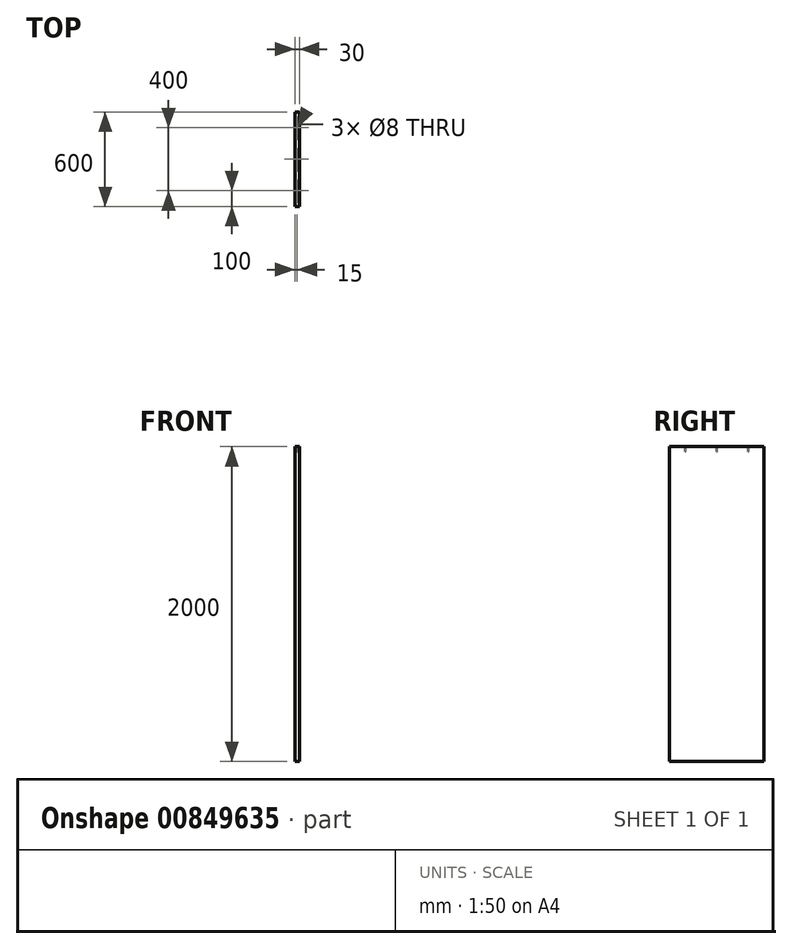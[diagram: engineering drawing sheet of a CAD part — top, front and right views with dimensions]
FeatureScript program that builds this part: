
annotation { "Feature Type Name" : "Feature", "Feature Type Description" : "" }
export const myFeature = defineFeature(function(context is Context, id is Id, definition is map)
    precondition{}
    {
        {
            var Q0;
            Q0=qCreatedBy(makeId("Right.planeOp"),FACE);
            var sketch = newSketch(context, id + "F0", { "sketchPlane" : qUnion([Q0])});
            skLineSegment(sketch, "E0.bottom", {"start": v(-600, 1000) * mm, "end": v(0, 1000) * mm});
            skLineSegment(sketch, "E0.top", {"start": v(-600, -1000) * mm, "end": v(0, -1000) * mm});
            skLineSegment(sketch, "E0.left", {"start": v(-600, 1000) * mm, "end": v(-600, -1000) * mm});
            skLineSegment(sketch, "E0.right", {"start": v(0, 1000) * mm, "end": v(0, -1000) * mm});
            skSolve(sketch);
        }
        {
            var Q0;
            Q0=makeQuery(id+"F0.imprint","IMPRINT",FACE,{"disambiguationData":[TD([[makeQuery(id+"F0.imprint","IMPRINT",EDGE,{"derivedFrom":sQuery(id+"F0.wireOp",EDGE,"E0.bottom")}),-1.0]])]});
            extrude(context, id + "F1", {"entities" : qUnion([Q0]), "endBound" : BoundingType.SYMMETRIC, "depth" : 30 * mm, "offsetDistance" : 25 * mm, "hasSecondDirection" : true, "secondDirectionOppositeDirection" : true, "secondDirectionDepth" : 15 * mm});
        }
        {
            var Q0;
            Q0=makeQuery(id+"F1.opExtrude","SWEPT_FACE",FACE,{"disambiguationData":[OSD([sQuery(id+"F0.wireOp",EDGE,"E0.bottom")])]});
            var sketch = newSketch(context, id + "F2", { "sketchPlane" : qUnion([Q0])});
            skLineSegment(sketch, "E1", {"start": v(0, 0) * mm, "end": v(0, -600) * mm, "construction": true});
            skPoint(sketch, "E2", {"position": v(0, -100) * mm});
            skPoint(sketch, "E3", {"position": v(0, -300) * mm});
            skPoint(sketch, "E4", {"position": v(0, -500) * mm});
            skLineSegment(sketch, "E5", {"start": v(-15, -300) * mm, "end": v(15, -300) * mm, "construction": true});
            skSolve(sketch);
        }
        {
            var Q0;
            Q0=sQuery(id+"F2.wireOp",VERTEX,"E2");
            var Q1;
            Q1=sQuery(id+"F2.wireOp",VERTEX,"E3");
            var Q2;
            Q2=sQuery(id+"F2.wireOp",VERTEX,"E4");
            var Q3;
            Q3=makeQuery(id+"F1.opExtrude","SWEPT_BODY",BODY,{"disambiguationData":[OSD([sQuery(id+"F0.wireOp",EDGE,"E0.bottom"),sQuery(id+"F0.wireOp",EDGE,"E0.top"),sQuery(id+"F0.wireOp",EDGE,"E0.left"),sQuery(id+"F0.wireOp",EDGE,"E0.right")])]});
            hole(context, id + "F3", {"style" : HoleStyle.SIMPLE, "endStyle" : HoleEndStyle.BLIND, "holeDiameter" : 8 * mm, "majorDiameter" : 5 * mm, "holeDepth" : 30 * mm, "isTappedThrough" : true, "tappedDepth" : 12 * mm, "tapClearance" : 3, "locations" : qUnion([Q0, Q1, Q2]), "scope" : qUnion([Q3])});
        }
    });
